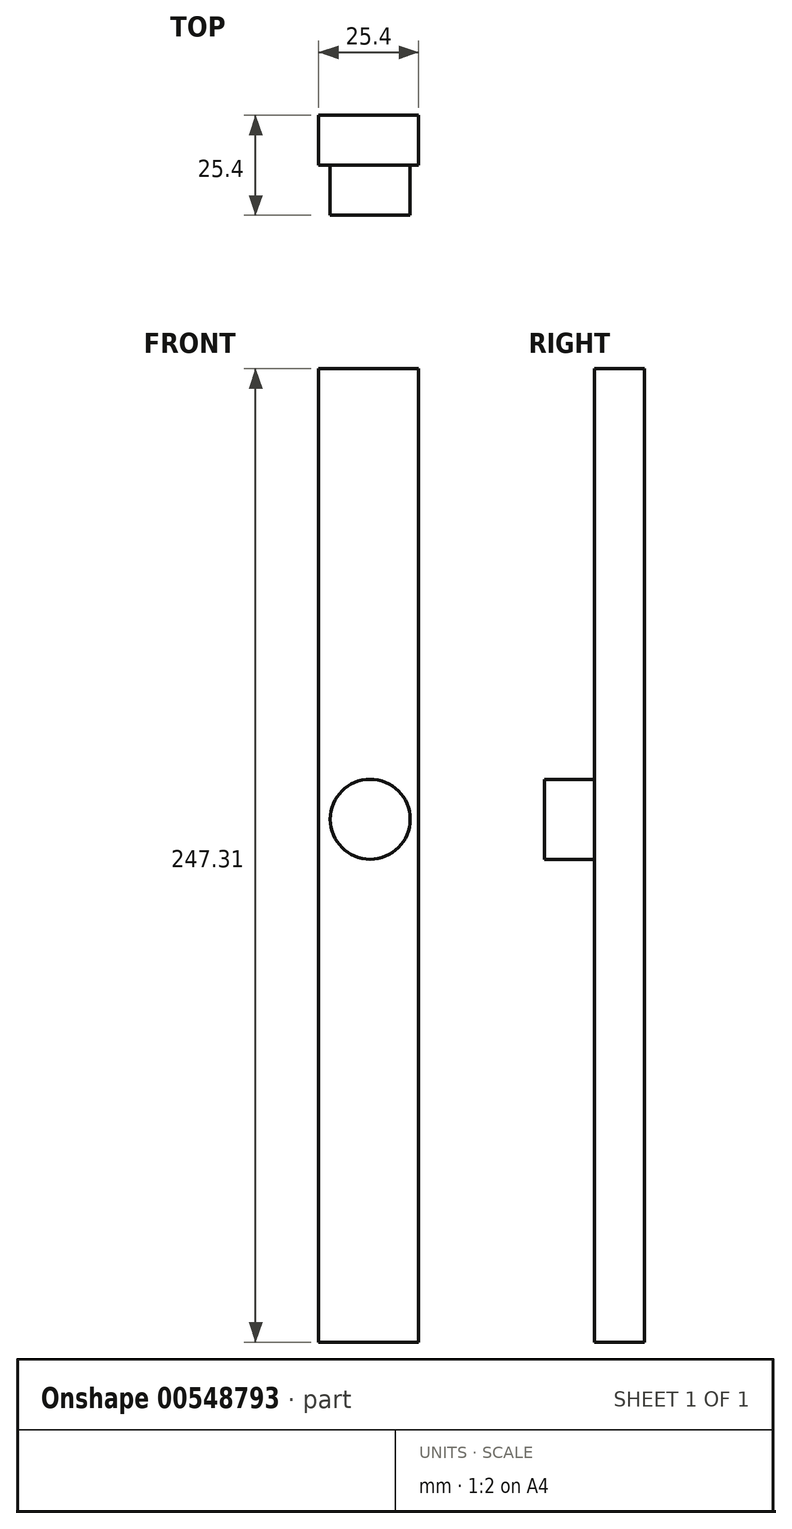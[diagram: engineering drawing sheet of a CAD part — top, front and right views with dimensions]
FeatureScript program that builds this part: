
annotation { "Feature Type Name" : "Feature", "Feature Type Description" : "" }
export const myFeature = defineFeature(function(context is Context, id is Id, definition is map)
    precondition{}
    {
        {
            var Q0;
            Q0=qCreatedBy(makeId("Front.planeOp"),FACE);
            var sketch = newSketch(context, id + "F0", { "sketchPlane" : qUnion([Q0])});
            skCircle(sketch, "E0", {"center": v(13.06, -14.34) * mm, "radius": 10.16 * mm});
            skLineSegment(sketch, "E1", {"start": v(25.4, 100.1) * mm, "end": v(25.4, -147.2) * mm});
            skLineSegment(sketch, "E2", {"start": v(0, 100.1) * mm, "end": v(0, -147.2) * mm});
            skLineSegment(sketch, "E3", {"start": v(0, -147.2) * mm, "end": v(0, 100.1) * mm});
            skLineSegment(sketch, "E4", {"start": v(25.4, 100.1) * mm, "end": v(0, 100.1) * mm});
            skLineSegment(sketch, "E5", {"start": v(25.4, -147.2) * mm, "end": v(0, -147.2) * mm});
            skSolve(sketch);
        }
        {
            var Q0;
            Q0=makeQuery(id+"F0.imprint","IMPRINT",FACE,{"disambiguationData":[TD([[makeQuery(id+"F0.imprint","IMPRINT",EDGE,{"derivedFrom":sQuery(id+"F0.wireOp",EDGE,"E0")}),-1.0]])]});
            extrude(context, id + "F1", {"entities" : qUnion([Q0]), "depth" : 12.7 * mm, "offsetDistance" : 25.4 * mm});
        }
        {
            var Q0;
            Q0=makeQuery(id+"F0.imprint","IMPRINT",FACE,{"disambiguationData":[TD([[makeQuery(id+"F0.imprint","IMPRINT",EDGE,{"derivedFrom":sQuery(id+"F0.wireOp",EDGE,"E0")}),1.0]])]});
            extrude(context, id + "F2", {"entities" : qUnion([Q0]), "operationType" : NewBodyOperationType.ADD, "depth" : 25.4 * mm, "offsetDistance" : 25.4 * mm});
        }
    });
